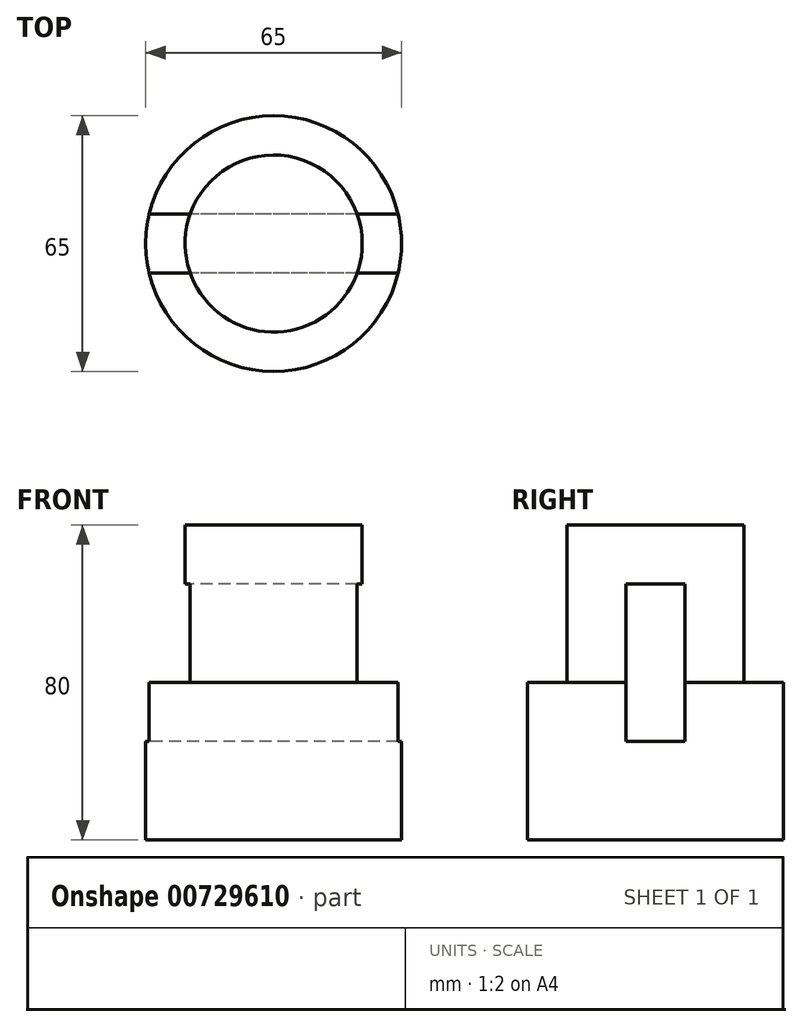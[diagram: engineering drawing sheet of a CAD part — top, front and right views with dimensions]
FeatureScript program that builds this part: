
annotation { "Feature Type Name" : "Feature", "Feature Type Description" : "" }
export const myFeature = defineFeature(function(context is Context, id is Id, definition is map)
    precondition{}
    {
        {
            var Q0;
            Q0=qCreatedBy(makeId("Top.planeOp"),FACE);
            var sketch = newSketch(context, id + "F0", { "sketchPlane" : qUnion([Q0])});
            skCircle(sketch, "E0", {"center": v(0, 0) * mm, "radius": 32.5 * mm});
            skSolve(sketch);
        }
        {
            var Q0;
            Q0 = qSketchRegion(id + "F0", true);
            extrude(context, id + "F1", {"entities" : qUnion([Q0]), "depth" : 40 * mm, "offsetDistance" : 25 * mm});
        }
        {
            var Q0;
            Q0=makeQuery(id+"F1.opExtrude","CAP_FACE",FACE,{"disambiguationData":[OSD([sQuery(id+"F0.wireOp",EDGE,"E0")])],"isStart":false});
            var sketch = newSketch(context, id + "F2", { "sketchPlane" : qUnion([Q0])});
            skCircle(sketch, "E1", {"center": v(0, 0) * mm, "radius": 22.5 * mm});
            skSolve(sketch);
        }
        {
            var Q0;
            Q0 = qSketchRegion(id + "F2", true);
            extrude(context, id + "F3", {"entities" : qUnion([Q0]), "operationType" : NewBodyOperationType.ADD, "depth" : 40 * mm, "offsetDistance" : 25 * mm});
        }
        {
            var Q0;
            Q0=qCreatedBy(makeId("Right.planeOp"),FACE);
            var sketch = newSketch(context, id + "F4", { "sketchPlane" : qUnion([Q0])});
            skLineSegment(sketch, "E2.bottom", {"start": v(-7.5, 65) * mm, "end": v(7.5, 65) * mm});
            skLineSegment(sketch, "E2.top", {"start": v(-7.5, 25) * mm, "end": v(7.5, 25) * mm});
            skLineSegment(sketch, "E2.left", {"start": v(-7.5, 65) * mm, "end": v(-7.5, 25) * mm});
            skLineSegment(sketch, "E2.right", {"start": v(7.5, 65) * mm, "end": v(7.5, 25) * mm});
            skSolve(sketch);
        }
        {
            var Q0;
            Q0 = qSketchRegion(id + "F4", true);
            extrude(context, id + "F5", {"entities" : qUnion([Q0]), "operationType" : NewBodyOperationType.REMOVE, "endBound" : BoundingType.SYMMETRIC, "depth" : 65 * mm, "offsetDistance" : 25 * mm});
        }
    });
